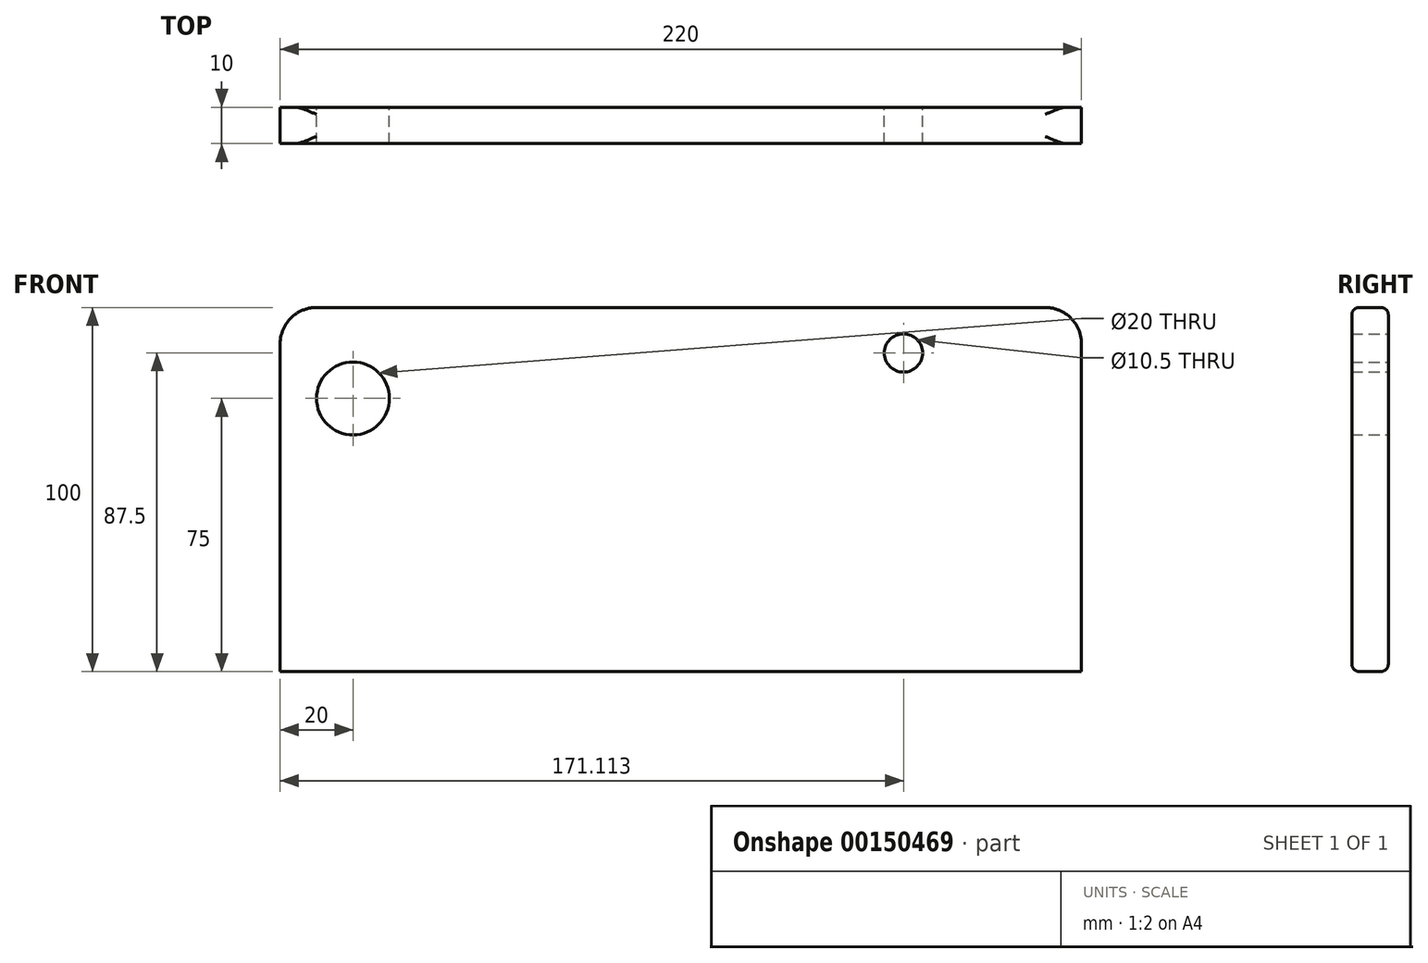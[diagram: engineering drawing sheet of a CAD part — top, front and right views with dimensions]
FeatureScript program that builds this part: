
annotation { "Feature Type Name" : "Feature", "Feature Type Description" : "" }
export const myFeature = defineFeature(function(context is Context, id is Id, definition is map)
    precondition{}
    {
        {
            var Q0;
            Q0=qCreatedBy(makeId("Front.planeOp"),FACE);
            var sketch = newSketch(context, id + "F0", { "sketchPlane" : qUnion([Q0])});
            skLineSegment(sketch, "E0.bottom", {"start": v(0, 0) * mm, "end": v(220, 0) * mm});
            skLineSegment(sketch, "E0.top", {"start": v(10, 100) * mm, "end": v(210, 100) * mm});
            skLineSegment(sketch, "E0.left", {"start": v(0, 0) * mm, "end": v(0, 90) * mm});
            skLineSegment(sketch, "E0.right", {"start": v(220, 0) * mm, "end": v(220, 90) * mm});
            skLineSegment(sketch, "E1.bottom", {"start": v(220, 0) * mm, "end": v(20, 0) * mm, "construction": true});
            skLineSegment(sketch, "E1.top", {"start": v(220, 75) * mm, "end": v(20, 75) * mm, "construction": true});
            skLineSegment(sketch, "E1.left", {"start": v(220, 0) * mm, "end": v(220, 75) * mm, "construction": true});
            skLineSegment(sketch, "E1.right", {"start": v(20, 0) * mm, "end": v(20, 75) * mm, "construction": true});
            skCircle(sketch, "E2", {"center": v(20, 75) * mm, "radius": 10 * mm});
            skPoint(sketch, "E3.visualSharp", {"position": v(0, 100) * mm});
            skArc(sketch, "E3.filletArc", {"start": v(10, 100) * mm, "mid": v(2.93, 97.07) * mm, "end": v(0, 90) * mm});
            skPoint(sketch, "E4.visualSharp", {"position": v(220, 100) * mm});
            skArc(sketch, "E4.filletArc", {"start": v(220, 90) * mm, "mid": v(217.07, 97.07) * mm, "end": v(210, 100) * mm});
            skSolve(sketch);
        }
        {
            var Q0;
            Q0=makeQuery(id+"F0.imprint","IMPRINT",FACE,{"disambiguationData":[TD([[makeQuery(id+"F0.imprint","IMPRINT",EDGE,{"derivedFrom":sQuery(id+"F0.wireOp",EDGE,"E0.bottom")}),1.0]])]});
            extrude(context, id + "F1", {"entities" : qUnion([Q0]), "depth" : 10 * mm});
        }
        {
            var Q0;
            Q0=makeQuery(id+"F1.opExtrude","CAP_EDGE",EDGE,{"disambiguationData":[OSD([sQuery(id+"F0.wireOp",EDGE,"E0.top")])],"isStart":false});
            var Q1;
            Q1=makeQuery(id+"F1.opExtrude","CAP_EDGE",EDGE,{"disambiguationData":[OSD([sQuery(id+"F0.wireOp",EDGE,"E0.top")])],"isStart":true});
            var Q2;
            Q2=makeQuery(id+"F1.opExtrude","CAP_EDGE",EDGE,{"disambiguationData":[OSD([sQuery(id+"F0.wireOp",EDGE,"E0.bottom")])],"isStart":false});
            var Q3;
            Q3=makeQuery(id+"F1.opExtrude","CAP_EDGE",EDGE,{"disambiguationData":[OSD([sQuery(id+"F0.wireOp",EDGE,"E0.bottom")])],"isStart":true});
            fillet(context, id + "F2", {"entities" : qUnion([Q0, Q1, Q2, Q3]), "radius" : 2 * mm, "allowEdgeOverflow" : false});
        }
        {
            var Q0;
            Q0=makeQuery(id+"F1.opExtrude","CAP_FACE",FACE,{"disambiguationData":[OSD([sQuery(id+"F0.wireOp",EDGE,"E0.bottom"),sQuery(id+"F0.wireOp",EDGE,"E0.top"),sQuery(id+"F0.wireOp",EDGE,"E0.left"),sQuery(id+"F0.wireOp",EDGE,"E0.right"),sQuery(id+"F0.wireOp",EDGE,"E2"),sQuery(id+"F0.wireOp",EDGE,"E3.filletArc"),sQuery(id+"F0.wireOp",EDGE,"E4.filletArc")])],"isStart":false});
            var sketch = newSketch(context, id + "F3", { "sketchPlane" : qUnion([Q0])});
            skPoint(sketch, "E5", {"position": v(171.11, 87.5) * mm});
            skSolve(sketch);
        }
        {
            var Q0;
            Q0=sQuery(id+"F3.wireOp",VERTEX,"E5");
            var Q1;
            Q1=makeQuery(id+"F1.opExtrude","SWEPT_BODY",BODY,{"disambiguationData":[OSD([sQuery(id+"F0.wireOp",EDGE,"E0.bottom"),sQuery(id+"F0.wireOp",EDGE,"E0.top"),sQuery(id+"F0.wireOp",EDGE,"E0.left"),sQuery(id+"F0.wireOp",EDGE,"E0.right"),sQuery(id+"F0.wireOp",EDGE,"E2"),sQuery(id+"F0.wireOp",EDGE,"E3.filletArc"),sQuery(id+"F0.wireOp",EDGE,"E4.filletArc")])]});
            hole(context, id + "F4", {"style" : HoleStyle.SIMPLE, "endStyle" : HoleEndStyle.THROUGH, "standardTappedOrClearance" : lookupTablePath({ "standard" : "ISO", "engagement" : "75%", "pitch" : "1.5 mm", "size" : "M12", "type" : "Tapped" }), "standardBlindInLast" : lookupTablePath({ "standard" : "ISO", "engagement" : "75%", "pitch" : "1.5 mm", "size" : "M12", "type" : "Tapped" }), "holeDiameter" : 10.5 * mm, "locations" : qUnion([Q0]), "scope" : qUnion([Q1]), "isTappedThrough" : true, "majorDiameter" : 12 * mm, "showTappedDepth" : true, "startStyle" : HoleStartStyle.PART});
        }
    });
